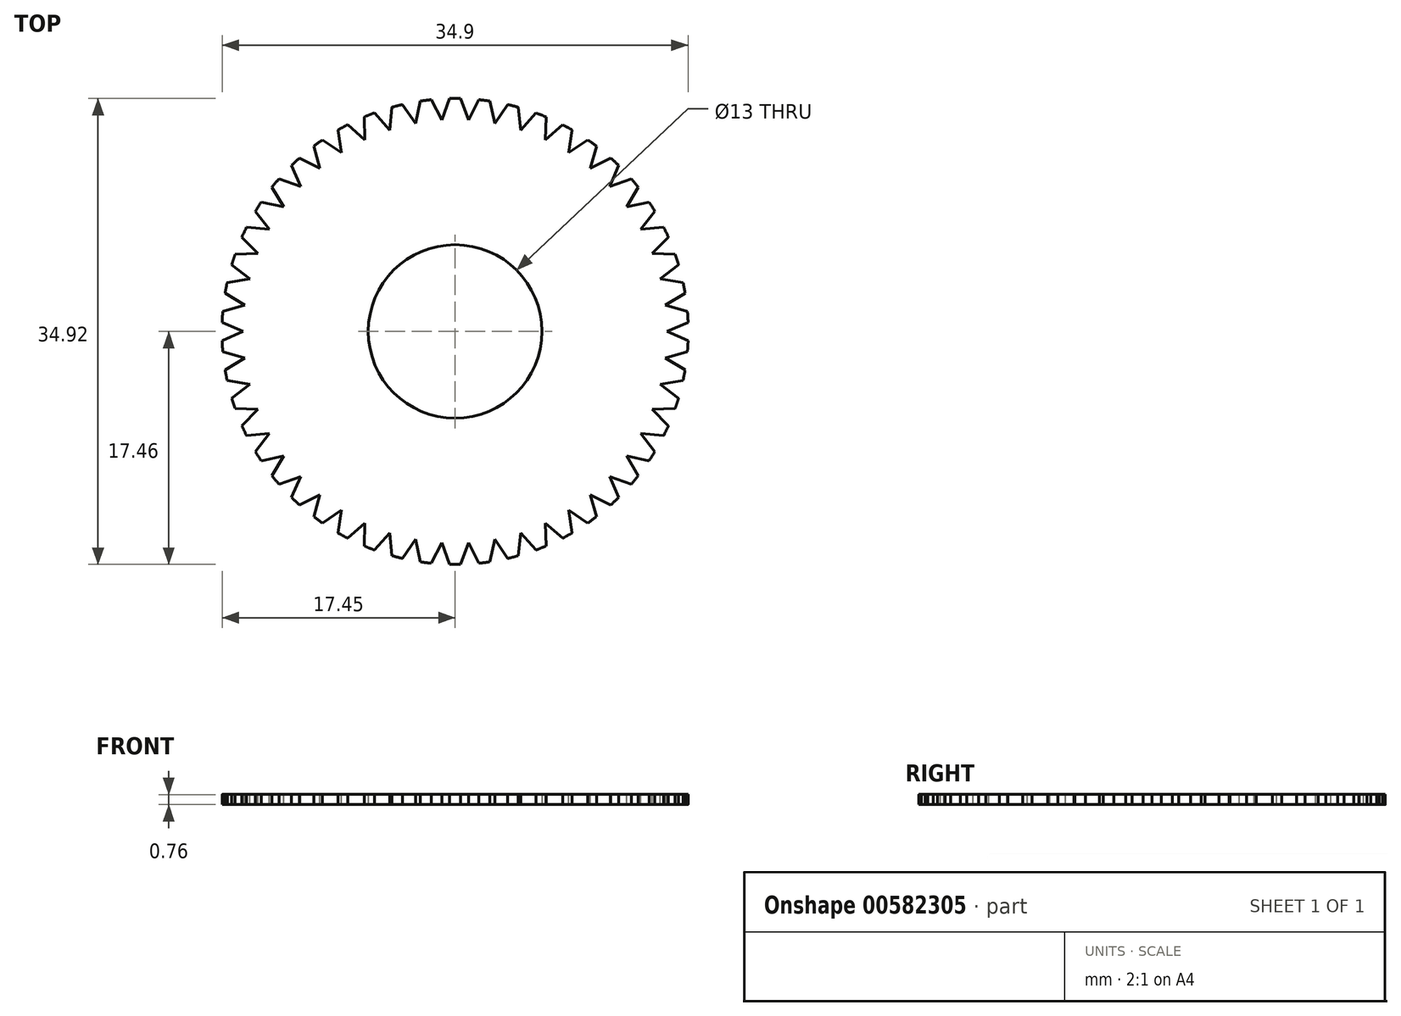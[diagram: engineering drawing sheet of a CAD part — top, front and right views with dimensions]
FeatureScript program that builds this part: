
annotation { "Feature Type Name" : "Feature", "Feature Type Description" : "" }
export const myFeature = defineFeature(function(context is Context, id is Id, definition is map)
    precondition{}
    {
        {
            var Q0;
            Q0=qCreatedBy(makeId("Top.planeOp"),FACE);
            var sketch = newSketch(context, id + "F0", { "sketchPlane" : qUnion([Q0])});
            skCircle(sketch, "E0", {"center": v(0, 0) * mm, "radius": 17.46 * mm});
            skCircle(sketch, "E1", {"center": v(0, 0) * mm, "radius": 6.5 * mm});
            skSolve(sketch);
        }
        {
            var Q0;
            Q0=makeQuery(id+"F0.imprint","IMPRINT",FACE,{"disambiguationData":[TD([[makeQuery(id+"F0.imprint","IMPRINT",EDGE,{"derivedFrom":sQuery(id+"F0.wireOp",EDGE,"E0")}),1.0]])]});
            extrude(context, id + "F1", {"entities" : qUnion([Q0]), "depth" : 0.76 * mm, "offsetDistance" : 25.4 * mm});
        }
        {
            var Q0;
            Q0=makeQuery(id+"F1.opExtrude","CAP_FACE",FACE,{"disambiguationData":[OSD([sQuery(id+"F0.wireOp",EDGE,"E0"),sQuery(id+"F0.wireOp",EDGE,"E1")])],"isStart":false});
            var sketch = newSketch(context, id + "F2", { "sketchPlane" : qUnion([Q0])});
            skLineSegment(sketch, "E2", {"start": v(0, 0) * mm, "end": v(17.46, 0) * mm, "construction": true});
            skLineSegment(sketch, "E3", {"start": v(15.88, 0) * mm, "end": v(17.45, 0.69) * mm});
            skArc(sketch, "E4.0", {"start": v(17.45, -0.69) * mm, "mid": v(17.46, 0) * mm, "end": v(17.45, 0.69) * mm});
            skArc(sketch, "E5.0", {"start": v(17.46, 0) * mm, "mid": v(17.46, 0.34) * mm, "end": v(17.45, 0.69) * mm});
            skLineSegment(sketch, "E6.MirrorCS", {"start": v(15.88, 0) * mm, "end": v(17.45, -0.69) * mm});
            skArc(sketch, "E7.MirrorCS", {"start": v(17.46, 0) * mm, "mid": v(17.46, -0.34) * mm, "end": v(17.45, -0.69) * mm});
            skLineSegment(sketch, "E8.1.0", {"start": v(15.75, 1.99) * mm, "end": v(17.23, 2.87) * mm});
            skArc(sketch, "E8.1.1", {"start": v(17.32, 2.19) * mm, "mid": v(17.28, 2.53) * mm, "end": v(17.23, 2.87) * mm});
            skArc(sketch, "E8.1.2", {"start": v(17.32, 2.19) * mm, "mid": v(17.36, 1.85) * mm, "end": v(17.4, 1.5) * mm});
            skLineSegment(sketch, "E8.1.3", {"start": v(15.75, 1.99) * mm, "end": v(17.4, 1.5) * mm});
            skLineSegment(sketch, "E8.2.0", {"start": v(15.38, 3.95) * mm, "end": v(16.73, 5) * mm});
            skArc(sketch, "E8.2.1", {"start": v(16.91, 4.34) * mm, "mid": v(16.83, 4.67) * mm, "end": v(16.73, 5) * mm});
            skArc(sketch, "E8.2.2", {"start": v(16.91, 4.34) * mm, "mid": v(17, 4) * mm, "end": v(17.07, 3.67) * mm});
            skLineSegment(sketch, "E8.2.3", {"start": v(15.38, 3.95) * mm, "end": v(17.07, 3.67) * mm});
            skLineSegment(sketch, "E8.3.0", {"start": v(14.76, 5.84) * mm, "end": v(15.97, 7.06) * mm});
            skArc(sketch, "E8.3.1", {"start": v(16.24, 6.43) * mm, "mid": v(16.1, 6.75) * mm, "end": v(15.97, 7.06) * mm});
            skArc(sketch, "E8.3.2", {"start": v(16.24, 6.43) * mm, "mid": v(16.36, 6.1) * mm, "end": v(16.48, 5.78) * mm});
            skLineSegment(sketch, "E8.3.3", {"start": v(14.76, 5.84) * mm, "end": v(16.48, 5.78) * mm});
            skLineSegment(sketch, "E8.4.0", {"start": v(13.91, 7.65) * mm, "end": v(14.96, 9) * mm});
            skArc(sketch, "E8.4.1", {"start": v(15.3, 8.41) * mm, "mid": v(15.13, 8.71) * mm, "end": v(14.96, 9) * mm});
            skArc(sketch, "E8.4.2", {"start": v(15.3, 8.41) * mm, "mid": v(15.47, 8.1) * mm, "end": v(15.62, 7.8) * mm});
            skLineSegment(sketch, "E8.4.3", {"start": v(13.91, 7.65) * mm, "end": v(15.62, 7.8) * mm});
            skLineSegment(sketch, "E8.5.0", {"start": v(12.84, 9.33) * mm, "end": v(13.71, 10.81) * mm});
            skArc(sketch, "E8.5.1", {"start": v(14.13, 10.26) * mm, "mid": v(13.92, 10.54) * mm, "end": v(13.71, 10.81) * mm});
            skArc(sketch, "E8.5.2", {"start": v(14.13, 10.26) * mm, "mid": v(14.33, 9.98) * mm, "end": v(14.52, 9.7) * mm});
            skLineSegment(sketch, "E8.5.3", {"start": v(12.84, 9.33) * mm, "end": v(14.52, 9.7) * mm});
            skLineSegment(sketch, "E8.6.0", {"start": v(11.57, 10.87) * mm, "end": v(12.25, 12.45) * mm});
            skArc(sketch, "E8.6.1", {"start": v(12.73, 11.95) * mm, "mid": v(12.5, 12.2) * mm, "end": v(12.25, 12.45) * mm});
            skArc(sketch, "E8.6.2", {"start": v(12.73, 11.95) * mm, "mid": v(12.96, 11.7) * mm, "end": v(13.2, 11.44) * mm});
            skLineSegment(sketch, "E8.6.3", {"start": v(11.57, 10.87) * mm, "end": v(13.2, 11.44) * mm});
            skLineSegment(sketch, "E8.7.0", {"start": v(10.12, 12.23) * mm, "end": v(10.6, 13.88) * mm});
            skArc(sketch, "E8.7.1", {"start": v(11.13, 13.46) * mm, "mid": v(10.86, 13.67) * mm, "end": v(10.6, 13.88) * mm});
            skArc(sketch, "E8.7.2", {"start": v(11.13, 13.46) * mm, "mid": v(11.4, 13.23) * mm, "end": v(11.65, 13) * mm});
            skLineSegment(sketch, "E8.7.3", {"start": v(10.12, 12.23) * mm, "end": v(11.65, 13) * mm});
            skLineSegment(sketch, "E8.8.0", {"start": v(8.5, 13.4) * mm, "end": v(8.77, 15.1) * mm});
            skArc(sketch, "E8.8.1", {"start": v(9.36, 14.74) * mm, "mid": v(9.07, 14.93) * mm, "end": v(8.77, 15.1) * mm});
            skArc(sketch, "E8.8.2", {"start": v(9.36, 14.74) * mm, "mid": v(9.65, 14.56) * mm, "end": v(9.93, 14.36) * mm});
            skLineSegment(sketch, "E8.8.3", {"start": v(8.5, 13.4) * mm, "end": v(9.93, 14.36) * mm});
            skLineSegment(sketch, "E8.9.0", {"start": v(6.76, 14.36) * mm, "end": v(6.8, 16.08) * mm});
            skArc(sketch, "E8.9.1", {"start": v(7.44, 15.8) * mm, "mid": v(7.12, 15.94) * mm, "end": v(6.8, 16.08) * mm});
            skArc(sketch, "E8.9.2", {"start": v(7.44, 15.8) * mm, "mid": v(7.74, 15.65) * mm, "end": v(8.05, 15.5) * mm});
            skLineSegment(sketch, "E8.9.3", {"start": v(6.76, 14.36) * mm, "end": v(8.05, 15.5) * mm});
            skLineSegment(sketch, "E8.10.0", {"start": v(4.9, 15.1) * mm, "end": v(4.74, 16.8) * mm});
            skArc(sketch, "E8.10.1", {"start": v(5.4, 16.6) * mm, "mid": v(5.07, 16.71) * mm, "end": v(4.74, 16.8) * mm});
            skArc(sketch, "E8.10.2", {"start": v(5.4, 16.6) * mm, "mid": v(5.72, 16.5) * mm, "end": v(6.05, 16.38) * mm});
            skLineSegment(sketch, "E8.10.3", {"start": v(4.9, 15.1) * mm, "end": v(6.05, 16.38) * mm});
            skLineSegment(sketch, "E8.11.0", {"start": v(2.97, 15.6) * mm, "end": v(2.6, 17.27) * mm});
            skArc(sketch, "E8.11.1", {"start": v(3.27, 17.15) * mm, "mid": v(2.93, 17.21) * mm, "end": v(2.6, 17.27) * mm});
            skArc(sketch, "E8.11.2", {"start": v(3.27, 17.15) * mm, "mid": v(3.6, 17.09) * mm, "end": v(3.94, 17.01) * mm});
            skLineSegment(sketch, "E8.11.3", {"start": v(2.97, 15.6) * mm, "end": v(3.94, 17.01) * mm});
            skLineSegment(sketch, "E8.12.0", {"start": v(1, 15.84) * mm, "end": v(0.41, 17.46) * mm});
            skArc(sketch, "E8.12.1", {"start": v(1.1, 17.43) * mm, "mid": v(0.75, 17.45) * mm, "end": v(0.41, 17.46) * mm});
            skArc(sketch, "E8.12.2", {"start": v(1.1, 17.43) * mm, "mid": v(1.44, 17.4) * mm, "end": v(1.78, 17.37) * mm});
            skLineSegment(sketch, "E8.12.3", {"start": v(1, 15.84) * mm, "end": v(1.78, 17.37) * mm});
            skLineSegment(sketch, "E8.13.0", {"start": v(-1, 15.84) * mm, "end": v(-1.78, 17.37) * mm});
            skArc(sketch, "E8.13.1", {"start": v(-1.1, 17.43) * mm, "mid": v(-1.44, 17.4) * mm, "end": v(-1.78, 17.37) * mm});
            skArc(sketch, "E8.13.2", {"start": v(-1.1, 17.43) * mm, "mid": v(-0.75, 17.45) * mm, "end": v(-0.41, 17.46) * mm});
            skLineSegment(sketch, "E8.13.3", {"start": v(-1, 15.84) * mm, "end": v(-0.41, 17.46) * mm});
            skLineSegment(sketch, "E8.14.0", {"start": v(-2.97, 15.6) * mm, "end": v(-3.94, 17.01) * mm});
            skArc(sketch, "E8.14.1", {"start": v(-3.27, 17.15) * mm, "mid": v(-3.6, 17.09) * mm, "end": v(-3.94, 17.01) * mm});
            skArc(sketch, "E8.14.2", {"start": v(-3.27, 17.15) * mm, "mid": v(-2.93, 17.21) * mm, "end": v(-2.6, 17.27) * mm});
            skLineSegment(sketch, "E8.14.3", {"start": v(-2.97, 15.6) * mm, "end": v(-2.6, 17.27) * mm});
            skLineSegment(sketch, "E8.15.0", {"start": v(-4.9, 15.1) * mm, "end": v(-6.05, 16.38) * mm});
            skArc(sketch, "E8.15.1", {"start": v(-5.4, 16.6) * mm, "mid": v(-5.72, 16.5) * mm, "end": v(-6.05, 16.38) * mm});
            skArc(sketch, "E8.15.2", {"start": v(-5.4, 16.6) * mm, "mid": v(-5.07, 16.71) * mm, "end": v(-4.74, 16.8) * mm});
            skLineSegment(sketch, "E8.15.3", {"start": v(-4.9, 15.1) * mm, "end": v(-4.74, 16.8) * mm});
            skLineSegment(sketch, "E8.16.0", {"start": v(-6.76, 14.36) * mm, "end": v(-8.05, 15.5) * mm});
            skArc(sketch, "E8.16.1", {"start": v(-7.44, 15.8) * mm, "mid": v(-7.74, 15.65) * mm, "end": v(-8.05, 15.5) * mm});
            skArc(sketch, "E8.16.2", {"start": v(-7.44, 15.8) * mm, "mid": v(-7.12, 15.94) * mm, "end": v(-6.8, 16.08) * mm});
            skLineSegment(sketch, "E8.16.3", {"start": v(-6.76, 14.36) * mm, "end": v(-6.8, 16.08) * mm});
            skLineSegment(sketch, "E8.17.0", {"start": v(-8.5, 13.4) * mm, "end": v(-9.93, 14.36) * mm});
            skArc(sketch, "E8.17.1", {"start": v(-9.36, 14.74) * mm, "mid": v(-9.65, 14.56) * mm, "end": v(-9.93, 14.36) * mm});
            skArc(sketch, "E8.17.2", {"start": v(-9.36, 14.74) * mm, "mid": v(-9.07, 14.93) * mm, "end": v(-8.77, 15.1) * mm});
            skLineSegment(sketch, "E8.17.3", {"start": v(-8.5, 13.4) * mm, "end": v(-8.77, 15.1) * mm});
            skLineSegment(sketch, "E8.18.0", {"start": v(-10.12, 12.23) * mm, "end": v(-11.65, 13) * mm});
            skArc(sketch, "E8.18.1", {"start": v(-11.13, 13.46) * mm, "mid": v(-11.4, 13.23) * mm, "end": v(-11.65, 13) * mm});
            skArc(sketch, "E8.18.2", {"start": v(-11.13, 13.46) * mm, "mid": v(-10.86, 13.67) * mm, "end": v(-10.6, 13.88) * mm});
            skLineSegment(sketch, "E8.18.3", {"start": v(-10.12, 12.23) * mm, "end": v(-10.6, 13.88) * mm});
            skLineSegment(sketch, "E8.19.0", {"start": v(-11.57, 10.87) * mm, "end": v(-13.2, 11.44) * mm});
            skArc(sketch, "E8.19.1", {"start": v(-12.73, 11.95) * mm, "mid": v(-12.96, 11.7) * mm, "end": v(-13.2, 11.44) * mm});
            skArc(sketch, "E8.19.2", {"start": v(-12.73, 11.95) * mm, "mid": v(-12.5, 12.2) * mm, "end": v(-12.25, 12.45) * mm});
            skLineSegment(sketch, "E8.19.3", {"start": v(-11.57, 10.87) * mm, "end": v(-12.25, 12.45) * mm});
            skLineSegment(sketch, "E8.20.0", {"start": v(-12.84, 9.33) * mm, "end": v(-14.52, 9.7) * mm});
            skArc(sketch, "E8.20.1", {"start": v(-14.13, 10.26) * mm, "mid": v(-14.33, 9.98) * mm, "end": v(-14.52, 9.7) * mm});
            skArc(sketch, "E8.20.2", {"start": v(-14.13, 10.26) * mm, "mid": v(-13.92, 10.54) * mm, "end": v(-13.71, 10.81) * mm});
            skLineSegment(sketch, "E8.20.3", {"start": v(-12.84, 9.33) * mm, "end": v(-13.71, 10.81) * mm});
            skLineSegment(sketch, "E8.21.0", {"start": v(-13.91, 7.65) * mm, "end": v(-15.62, 7.8) * mm});
            skArc(sketch, "E8.21.1", {"start": v(-15.3, 8.41) * mm, "mid": v(-15.47, 8.1) * mm, "end": v(-15.62, 7.8) * mm});
            skArc(sketch, "E8.21.2", {"start": v(-15.3, 8.41) * mm, "mid": v(-15.13, 8.71) * mm, "end": v(-14.96, 9) * mm});
            skLineSegment(sketch, "E8.21.3", {"start": v(-13.91, 7.65) * mm, "end": v(-14.96, 9) * mm});
            skLineSegment(sketch, "E8.22.0", {"start": v(-14.76, 5.84) * mm, "end": v(-16.48, 5.78) * mm});
            skArc(sketch, "E8.22.1", {"start": v(-16.24, 6.43) * mm, "mid": v(-16.36, 6.1) * mm, "end": v(-16.48, 5.78) * mm});
            skArc(sketch, "E8.22.2", {"start": v(-16.24, 6.43) * mm, "mid": v(-16.1, 6.75) * mm, "end": v(-15.97, 7.06) * mm});
            skLineSegment(sketch, "E8.22.3", {"start": v(-14.76, 5.84) * mm, "end": v(-15.97, 7.06) * mm});
            skLineSegment(sketch, "E8.23.0", {"start": v(-15.38, 3.95) * mm, "end": v(-17.07, 3.67) * mm});
            skArc(sketch, "E8.23.1", {"start": v(-16.91, 4.34) * mm, "mid": v(-17, 4) * mm, "end": v(-17.07, 3.67) * mm});
            skArc(sketch, "E8.23.2", {"start": v(-16.91, 4.34) * mm, "mid": v(-16.83, 4.67) * mm, "end": v(-16.73, 5) * mm});
            skLineSegment(sketch, "E8.23.3", {"start": v(-15.38, 3.95) * mm, "end": v(-16.73, 5) * mm});
            skLineSegment(sketch, "E8.24.0", {"start": v(-15.75, 1.99) * mm, "end": v(-17.4, 1.5) * mm});
            skArc(sketch, "E8.24.1", {"start": v(-17.32, 2.19) * mm, "mid": v(-17.36, 1.85) * mm, "end": v(-17.4, 1.5) * mm});
            skArc(sketch, "E8.24.2", {"start": v(-17.32, 2.19) * mm, "mid": v(-17.28, 2.53) * mm, "end": v(-17.23, 2.87) * mm});
            skLineSegment(sketch, "E8.24.3", {"start": v(-15.75, 1.99) * mm, "end": v(-17.23, 2.87) * mm});
            skLineSegment(sketch, "E8.25.0", {"start": v(-15.88, 0) * mm, "end": v(-17.45, -0.69) * mm});
            skArc(sketch, "E8.25.1", {"start": v(-17.46, 0) * mm, "mid": v(-17.46, -0.34) * mm, "end": v(-17.45, -0.69) * mm});
            skArc(sketch, "E8.25.2", {"start": v(-17.46, 0) * mm, "mid": v(-17.46, 0.34) * mm, "end": v(-17.45, 0.69) * mm});
            skLineSegment(sketch, "E8.25.3", {"start": v(-15.88, 0) * mm, "end": v(-17.45, 0.69) * mm});
            skLineSegment(sketch, "E8.26.0", {"start": v(-15.75, -1.99) * mm, "end": v(-17.23, -2.87) * mm});
            skArc(sketch, "E8.26.1", {"start": v(-17.32, -2.19) * mm, "mid": v(-17.28, -2.53) * mm, "end": v(-17.23, -2.87) * mm});
            skArc(sketch, "E8.26.2", {"start": v(-17.32, -2.19) * mm, "mid": v(-17.36, -1.85) * mm, "end": v(-17.4, -1.5) * mm});
            skLineSegment(sketch, "E8.26.3", {"start": v(-15.75, -1.99) * mm, "end": v(-17.4, -1.5) * mm});
            skLineSegment(sketch, "E8.27.0", {"start": v(-15.38, -3.95) * mm, "end": v(-16.73, -5) * mm});
            skArc(sketch, "E8.27.1", {"start": v(-16.91, -4.34) * mm, "mid": v(-16.83, -4.67) * mm, "end": v(-16.73, -5) * mm});
            skArc(sketch, "E8.27.2", {"start": v(-16.91, -4.34) * mm, "mid": v(-17, -4) * mm, "end": v(-17.07, -3.67) * mm});
            skLineSegment(sketch, "E8.27.3", {"start": v(-15.38, -3.95) * mm, "end": v(-17.07, -3.67) * mm});
            skLineSegment(sketch, "E8.28.0", {"start": v(-14.76, -5.84) * mm, "end": v(-15.97, -7.06) * mm});
            skArc(sketch, "E8.28.1", {"start": v(-16.24, -6.43) * mm, "mid": v(-16.1, -6.75) * mm, "end": v(-15.97, -7.06) * mm});
            skArc(sketch, "E8.28.2", {"start": v(-16.24, -6.43) * mm, "mid": v(-16.36, -6.1) * mm, "end": v(-16.48, -5.78) * mm});
            skLineSegment(sketch, "E8.28.3", {"start": v(-14.76, -5.84) * mm, "end": v(-16.48, -5.78) * mm});
            skLineSegment(sketch, "E8.29.0", {"start": v(-13.91, -7.65) * mm, "end": v(-14.96, -9) * mm});
            skArc(sketch, "E8.29.1", {"start": v(-15.3, -8.41) * mm, "mid": v(-15.13, -8.71) * mm, "end": v(-14.96, -9) * mm});
            skArc(sketch, "E8.29.2", {"start": v(-15.3, -8.41) * mm, "mid": v(-15.47, -8.1) * mm, "end": v(-15.62, -7.8) * mm});
            skLineSegment(sketch, "E8.29.3", {"start": v(-13.91, -7.65) * mm, "end": v(-15.62, -7.8) * mm});
            skLineSegment(sketch, "E8.30.0", {"start": v(-12.84, -9.33) * mm, "end": v(-13.71, -10.81) * mm});
            skArc(sketch, "E8.30.1", {"start": v(-14.13, -10.26) * mm, "mid": v(-13.92, -10.54) * mm, "end": v(-13.71, -10.81) * mm});
            skArc(sketch, "E8.30.2", {"start": v(-14.13, -10.26) * mm, "mid": v(-14.33, -9.98) * mm, "end": v(-14.52, -9.7) * mm});
            skLineSegment(sketch, "E8.30.3", {"start": v(-12.84, -9.33) * mm, "end": v(-14.52, -9.7) * mm});
            skLineSegment(sketch, "E8.31.0", {"start": v(-11.57, -10.87) * mm, "end": v(-12.25, -12.45) * mm});
            skArc(sketch, "E8.31.1", {"start": v(-12.73, -11.95) * mm, "mid": v(-12.5, -12.2) * mm, "end": v(-12.25, -12.45) * mm});
            skArc(sketch, "E8.31.2", {"start": v(-12.73, -11.95) * mm, "mid": v(-12.96, -11.7) * mm, "end": v(-13.2, -11.44) * mm});
            skLineSegment(sketch, "E8.31.3", {"start": v(-11.57, -10.87) * mm, "end": v(-13.2, -11.44) * mm});
            skLineSegment(sketch, "E8.32.0", {"start": v(-10.12, -12.23) * mm, "end": v(-10.6, -13.88) * mm});
            skArc(sketch, "E8.32.1", {"start": v(-11.13, -13.46) * mm, "mid": v(-10.86, -13.67) * mm, "end": v(-10.6, -13.88) * mm});
            skArc(sketch, "E8.32.2", {"start": v(-11.13, -13.46) * mm, "mid": v(-11.4, -13.23) * mm, "end": v(-11.65, -13) * mm});
            skLineSegment(sketch, "E8.32.3", {"start": v(-10.12, -12.23) * mm, "end": v(-11.65, -13) * mm});
            skLineSegment(sketch, "E8.33.0", {"start": v(-8.5, -13.4) * mm, "end": v(-8.77, -15.1) * mm});
            skArc(sketch, "E8.33.1", {"start": v(-9.36, -14.74) * mm, "mid": v(-9.07, -14.93) * mm, "end": v(-8.77, -15.1) * mm});
            skArc(sketch, "E8.33.2", {"start": v(-9.36, -14.74) * mm, "mid": v(-9.65, -14.56) * mm, "end": v(-9.93, -14.36) * mm});
            skLineSegment(sketch, "E8.33.3", {"start": v(-8.5, -13.4) * mm, "end": v(-9.93, -14.36) * mm});
            skLineSegment(sketch, "E8.34.0", {"start": v(-6.76, -14.36) * mm, "end": v(-6.8, -16.08) * mm});
            skArc(sketch, "E8.34.1", {"start": v(-7.44, -15.8) * mm, "mid": v(-7.12, -15.94) * mm, "end": v(-6.8, -16.08) * mm});
            skArc(sketch, "E8.34.2", {"start": v(-7.44, -15.8) * mm, "mid": v(-7.74, -15.65) * mm, "end": v(-8.05, -15.5) * mm});
            skLineSegment(sketch, "E8.34.3", {"start": v(-6.76, -14.36) * mm, "end": v(-8.05, -15.5) * mm});
            skLineSegment(sketch, "E8.35.0", {"start": v(-4.9, -15.1) * mm, "end": v(-4.74, -16.8) * mm});
            skArc(sketch, "E8.35.1", {"start": v(-5.4, -16.6) * mm, "mid": v(-5.07, -16.71) * mm, "end": v(-4.74, -16.8) * mm});
            skArc(sketch, "E8.35.2", {"start": v(-5.4, -16.6) * mm, "mid": v(-5.72, -16.5) * mm, "end": v(-6.05, -16.38) * mm});
            skLineSegment(sketch, "E8.35.3", {"start": v(-4.9, -15.1) * mm, "end": v(-6.05, -16.38) * mm});
            skLineSegment(sketch, "E8.36.0", {"start": v(-2.97, -15.6) * mm, "end": v(-2.6, -17.27) * mm});
            skArc(sketch, "E8.36.1", {"start": v(-3.27, -17.15) * mm, "mid": v(-2.93, -17.21) * mm, "end": v(-2.6, -17.27) * mm});
            skArc(sketch, "E8.36.2", {"start": v(-3.27, -17.15) * mm, "mid": v(-3.6, -17.09) * mm, "end": v(-3.94, -17.01) * mm});
            skLineSegment(sketch, "E8.36.3", {"start": v(-2.97, -15.6) * mm, "end": v(-3.94, -17.01) * mm});
            skLineSegment(sketch, "E8.37.0", {"start": v(-1, -15.84) * mm, "end": v(-0.41, -17.46) * mm});
            skArc(sketch, "E8.37.1", {"start": v(-1.1, -17.43) * mm, "mid": v(-0.75, -17.45) * mm, "end": v(-0.41, -17.46) * mm});
            skArc(sketch, "E8.37.2", {"start": v(-1.1, -17.43) * mm, "mid": v(-1.44, -17.4) * mm, "end": v(-1.78, -17.37) * mm});
            skLineSegment(sketch, "E8.37.3", {"start": v(-1, -15.84) * mm, "end": v(-1.78, -17.37) * mm});
            skLineSegment(sketch, "E8.38.0", {"start": v(1, -15.84) * mm, "end": v(1.78, -17.37) * mm});
            skArc(sketch, "E8.38.1", {"start": v(1.1, -17.43) * mm, "mid": v(1.44, -17.4) * mm, "end": v(1.78, -17.37) * mm});
            skArc(sketch, "E8.38.2", {"start": v(1.1, -17.43) * mm, "mid": v(0.75, -17.45) * mm, "end": v(0.41, -17.46) * mm});
            skLineSegment(sketch, "E8.38.3", {"start": v(1, -15.84) * mm, "end": v(0.41, -17.46) * mm});
            skLineSegment(sketch, "E8.39.0", {"start": v(2.97, -15.6) * mm, "end": v(3.94, -17.01) * mm});
            skArc(sketch, "E8.39.1", {"start": v(3.27, -17.15) * mm, "mid": v(3.6, -17.09) * mm, "end": v(3.94, -17.01) * mm});
            skArc(sketch, "E8.39.2", {"start": v(3.27, -17.15) * mm, "mid": v(2.93, -17.21) * mm, "end": v(2.6, -17.27) * mm});
            skLineSegment(sketch, "E8.39.3", {"start": v(2.97, -15.6) * mm, "end": v(2.6, -17.27) * mm});
            skLineSegment(sketch, "E8.40.0", {"start": v(4.9, -15.1) * mm, "end": v(6.05, -16.38) * mm});
            skArc(sketch, "E8.40.1", {"start": v(5.4, -16.6) * mm, "mid": v(5.72, -16.5) * mm, "end": v(6.05, -16.38) * mm});
            skArc(sketch, "E8.40.2", {"start": v(5.4, -16.6) * mm, "mid": v(5.07, -16.71) * mm, "end": v(4.74, -16.8) * mm});
            skLineSegment(sketch, "E8.40.3", {"start": v(4.9, -15.1) * mm, "end": v(4.74, -16.8) * mm});
            skLineSegment(sketch, "E8.41.0", {"start": v(6.76, -14.36) * mm, "end": v(8.05, -15.5) * mm});
            skArc(sketch, "E8.41.1", {"start": v(7.44, -15.8) * mm, "mid": v(7.74, -15.65) * mm, "end": v(8.05, -15.5) * mm});
            skArc(sketch, "E8.41.2", {"start": v(7.44, -15.8) * mm, "mid": v(7.12, -15.94) * mm, "end": v(6.8, -16.08) * mm});
            skLineSegment(sketch, "E8.41.3", {"start": v(6.76, -14.36) * mm, "end": v(6.8, -16.08) * mm});
            skLineSegment(sketch, "E8.42.0", {"start": v(8.5, -13.4) * mm, "end": v(9.93, -14.36) * mm});
            skArc(sketch, "E8.42.1", {"start": v(9.36, -14.74) * mm, "mid": v(9.65, -14.56) * mm, "end": v(9.93, -14.36) * mm});
            skArc(sketch, "E8.42.2", {"start": v(9.36, -14.74) * mm, "mid": v(9.07, -14.93) * mm, "end": v(8.77, -15.1) * mm});
            skLineSegment(sketch, "E8.42.3", {"start": v(8.5, -13.4) * mm, "end": v(8.77, -15.1) * mm});
            skLineSegment(sketch, "E8.43.0", {"start": v(10.12, -12.23) * mm, "end": v(11.65, -13) * mm});
            skArc(sketch, "E8.43.1", {"start": v(11.13, -13.46) * mm, "mid": v(11.4, -13.23) * mm, "end": v(11.65, -13) * mm});
            skArc(sketch, "E8.43.2", {"start": v(11.13, -13.46) * mm, "mid": v(10.86, -13.67) * mm, "end": v(10.6, -13.88) * mm});
            skLineSegment(sketch, "E8.43.3", {"start": v(10.12, -12.23) * mm, "end": v(10.6, -13.88) * mm});
            skLineSegment(sketch, "E8.44.0", {"start": v(11.57, -10.87) * mm, "end": v(13.2, -11.44) * mm});
            skArc(sketch, "E8.44.1", {"start": v(12.73, -11.95) * mm, "mid": v(12.96, -11.7) * mm, "end": v(13.2, -11.44) * mm});
            skArc(sketch, "E8.44.2", {"start": v(12.73, -11.95) * mm, "mid": v(12.5, -12.2) * mm, "end": v(12.25, -12.45) * mm});
            skLineSegment(sketch, "E8.44.3", {"start": v(11.57, -10.87) * mm, "end": v(12.25, -12.45) * mm});
            skLineSegment(sketch, "E8.45.0", {"start": v(12.84, -9.33) * mm, "end": v(14.52, -9.7) * mm});
            skArc(sketch, "E8.45.1", {"start": v(14.13, -10.26) * mm, "mid": v(14.33, -9.98) * mm, "end": v(14.52, -9.7) * mm});
            skArc(sketch, "E8.45.2", {"start": v(14.13, -10.26) * mm, "mid": v(13.92, -10.54) * mm, "end": v(13.71, -10.81) * mm});
            skLineSegment(sketch, "E8.45.3", {"start": v(12.84, -9.33) * mm, "end": v(13.71, -10.81) * mm});
            skLineSegment(sketch, "E8.46.0", {"start": v(13.91, -7.65) * mm, "end": v(15.62, -7.8) * mm});
            skArc(sketch, "E8.46.1", {"start": v(15.3, -8.41) * mm, "mid": v(15.47, -8.1) * mm, "end": v(15.62, -7.8) * mm});
            skArc(sketch, "E8.46.2", {"start": v(15.3, -8.41) * mm, "mid": v(15.13, -8.71) * mm, "end": v(14.96, -9) * mm});
            skLineSegment(sketch, "E8.46.3", {"start": v(13.91, -7.65) * mm, "end": v(14.96, -9) * mm});
            skLineSegment(sketch, "E8.47.0", {"start": v(14.76, -5.84) * mm, "end": v(16.48, -5.78) * mm});
            skArc(sketch, "E8.47.1", {"start": v(16.24, -6.43) * mm, "mid": v(16.36, -6.1) * mm, "end": v(16.48, -5.78) * mm});
            skArc(sketch, "E8.47.2", {"start": v(16.24, -6.43) * mm, "mid": v(16.1, -6.75) * mm, "end": v(15.97, -7.06) * mm});
            skLineSegment(sketch, "E8.47.3", {"start": v(14.76, -5.84) * mm, "end": v(15.97, -7.06) * mm});
            skLineSegment(sketch, "E8.48.0", {"start": v(15.38, -3.95) * mm, "end": v(17.07, -3.67) * mm});
            skArc(sketch, "E8.48.1", {"start": v(16.91, -4.34) * mm, "mid": v(17, -4) * mm, "end": v(17.07, -3.67) * mm});
            skArc(sketch, "E8.48.2", {"start": v(16.91, -4.34) * mm, "mid": v(16.83, -4.67) * mm, "end": v(16.73, -5) * mm});
            skLineSegment(sketch, "E8.48.3", {"start": v(15.38, -3.95) * mm, "end": v(16.73, -5) * mm});
            skLineSegment(sketch, "E8.49.0", {"start": v(15.75, -1.99) * mm, "end": v(17.4, -1.5) * mm});
            skArc(sketch, "E8.49.1", {"start": v(17.32, -2.19) * mm, "mid": v(17.36, -1.85) * mm, "end": v(17.4, -1.5) * mm});
            skArc(sketch, "E8.49.2", {"start": v(17.32, -2.19) * mm, "mid": v(17.28, -2.53) * mm, "end": v(17.23, -2.87) * mm});
            skLineSegment(sketch, "E8.49.3", {"start": v(15.75, -1.99) * mm, "end": v(17.23, -2.87) * mm});
            skSolve(sketch);
        }
        {
            var Q0;
            Q0 = qSketchRegion(id + "F2", true);
            extrude(context, id + "F3", {"entities" : qUnion([Q0]), "operationType" : NewBodyOperationType.REMOVE, "endBound" : BoundingType.UP_TO_NEXT, "oppositeDirection" : true, "depth" : 25.4 * mm, "offsetDistance" : 25.4 * mm});
        }
    });
